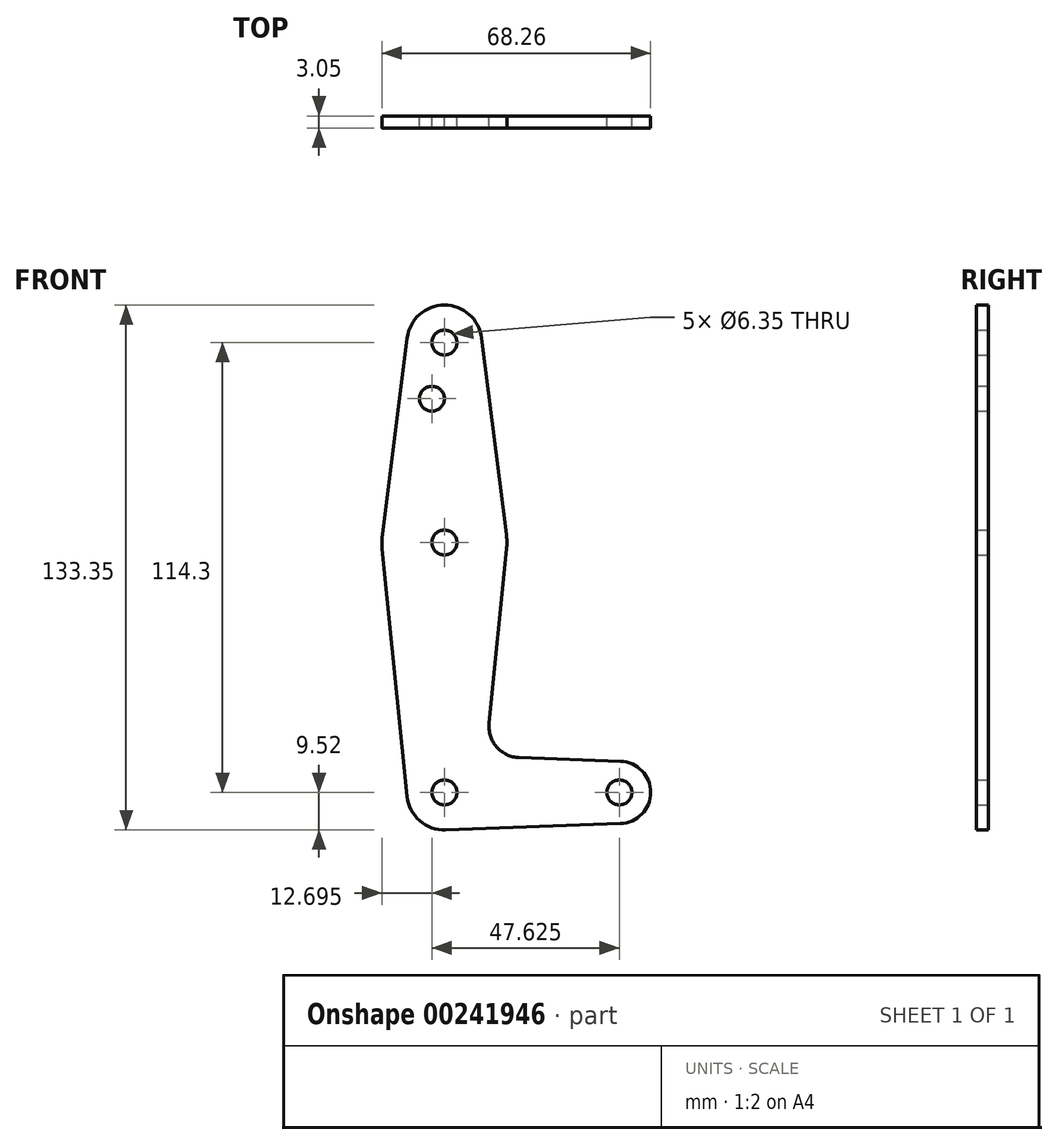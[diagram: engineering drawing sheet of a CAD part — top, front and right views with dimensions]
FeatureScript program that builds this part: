
annotation { "Feature Type Name" : "Feature", "Feature Type Description" : "" }
export const myFeature = defineFeature(function(context is Context, id is Id, definition is map)
    precondition{}
    {
        {
            var Q0;
            Q0=qCreatedBy(makeId("Front.planeOp"),FACE);
            var sketch = newSketch(context, id + "F0", { "sketchPlane" : qUnion([Q0])});
            skLineSegment(sketch, "E0", {"start": v(0, 114.3) * mm, "end": v(0, 0) * mm, "construction": true});
            skLineSegment(sketch, "E1", {"start": v(0, 0) * mm, "end": v(44.45, 0) * mm, "construction": true});
            skCircle(sketch, "E2", {"center": v(0, 63.5) * mm, "radius": 15.88 * mm});
            skCircle(sketch, "E3", {"center": v(0, 0) * mm, "radius": 3.18 * mm});
            skCircle(sketch, "E4", {"center": v(0, 0) * mm, "radius": 9.53 * mm});
            skCircle(sketch, "E5", {"center": v(44.45, 0) * mm, "radius": 3.18 * mm});
            skCircle(sketch, "E6", {"center": v(44.45, 0) * mm, "radius": 7.94 * mm});
            skCircle(sketch, "E7", {"center": v(0, 114.3) * mm, "radius": 3.18 * mm});
            skCircle(sketch, "E8", {"center": v(0, 114.3) * mm, "radius": 9.53 * mm});
            skCircle(sketch, "E9", {"center": v(0, 63.5) * mm, "radius": 3.18 * mm});
            skLineSegment(sketch, "E10", {"start": v(-9.45, 115.5) * mm, "end": v(-15.75, 65.48) * mm});
            skLineSegment(sketch, "E11", {"start": v(9.45, 115.5) * mm, "end": v(15.75, 65.48) * mm});
            skLineSegment(sketch, "E12", {"start": v(15.8, 61.91) * mm, "end": v(11.34, 17.6) * mm});
            skLineSegment(sketch, "E13", {"start": v(18.97, 8.85) * mm, "end": v(44.73, 7.93) * mm});
            skLineSegment(sketch, "E14", {"start": v(0.34, -9.52) * mm, "end": v(44.73, -7.93) * mm});
            skCircle(sketch, "E15", {"center": v(-3.17, 100.03) * mm, "radius": 3.18 * mm});
            skArc(sketch, "E16.filletArc", {"start": v(11.34, 17.6) * mm, "mid": v(13.26, 11.57) * mm, "end": v(18.97, 8.85) * mm});
            skLineSegment(sketch, "E17", {"start": v(-15.8, 61.91) * mm, "end": v(-9.48, -0.95) * mm});
            skSolve(sketch);
        }
        {
            var Q0;
            Q0=makeQuery(id+"F0.imprint","IMPRINT",FACE,{"disambiguationData":[TD([[makeQuery(id+"F0.imprint","IMPRINT",EDGE,{"derivedFrom":sQuery(id+"F0.wireOp",EDGE,"E7")}),-1.0]])]});
            var Q1;
            {var subQ1=sQuery(id+"F0.wireOp",EDGE,"E10");Q1=makeQuery(id+"F0.imprint","IMPRINT",FACE,{"disambiguationData":[TD([[makeQuery(id+"F0.imprint","IMPRINT",EDGE,{"derivedFrom":subQ1}),1.0]])]});}
            var Q2;
            Q2=makeQuery(id+"F0.imprint","IMPRINT",FACE,{"disambiguationData":[TD([[makeQuery(id+"F0.imprint","IMPRINT",EDGE,{"derivedFrom":sQuery(id+"F0.wireOp",EDGE,"E9")}),-1.0]])]});
            var Q3;
            {var subQ3=sQuery(id+"F0.wireOp",EDGE,"E12");Q3=makeQuery(id+"F0.imprint","IMPRINT",FACE,{"disambiguationData":[TD([[makeQuery(id+"F0.imprint","IMPRINT",EDGE,{"derivedFrom":subQ3}),-1.0]])]});}
            var Q4;
            Q4=makeQuery(id+"F0.imprint","IMPRINT",FACE,{"disambiguationData":[TD([[makeQuery(id+"F0.imprint","IMPRINT",EDGE,{"derivedFrom":sQuery(id+"F0.wireOp",EDGE,"E3")}),-1.0]])]});
            var Q5;
            Q5=makeQuery(id+"F0.imprint","IMPRINT",FACE,{"disambiguationData":[TD([[makeQuery(id+"F0.imprint","IMPRINT",EDGE,{"derivedFrom":sQuery(id+"F0.wireOp",EDGE,"E5")}),-1.0]])]});
            extrude(context, id + "F1", {"entities" : qUnion([Q0, Q1, Q2, Q3, Q4, Q5]), "depth" : 3.05 * mm});
        }
    });
